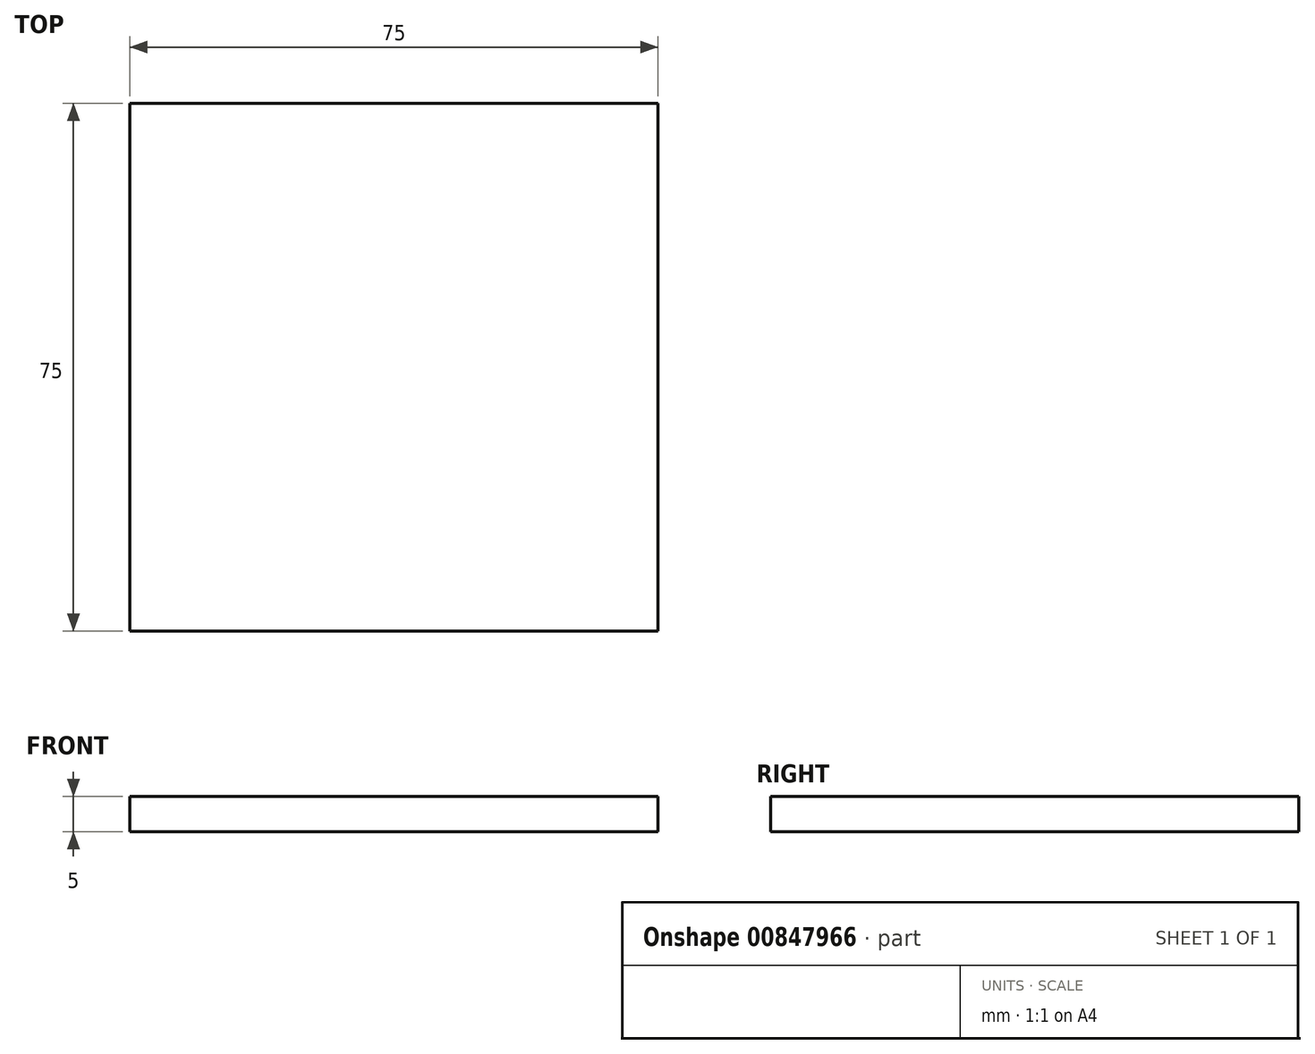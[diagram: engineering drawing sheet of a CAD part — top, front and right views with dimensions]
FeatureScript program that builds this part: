
annotation { "Feature Type Name" : "Feature", "Feature Type Description" : "" }
export const myFeature = defineFeature(function(context is Context, id is Id, definition is map)
    precondition{}
    {
        {
            var Q0;
            Q0=qCreatedBy(makeId("Top.planeOp"),FACE);
            var sketch = newSketch(context, id + "F0", { "sketchPlane" : qUnion([Q0])});
            skLineSegment(sketch, "E0.bottom", {"start": v(37.5, -37.5) * mm, "end": v(-37.5, -37.5) * mm});
            skLineSegment(sketch, "E0.top", {"start": v(37.5, 37.5) * mm, "end": v(-37.5, 37.5) * mm});
            skLineSegment(sketch, "E0.left", {"start": v(37.5, -37.5) * mm, "end": v(37.5, 37.5) * mm});
            skLineSegment(sketch, "E0.right", {"start": v(-37.5, -37.5) * mm, "end": v(-37.5, 37.5) * mm});
            skPoint(sketch, "E0.middle", {"position": v(0, 0) * mm});
            skSolve(sketch);
        }
        {
            var Q0;
            Q0 = qSketchRegion(id + "F0", true);
            extrude(context, id + "F1", {"entities" : qUnion([Q0]), "depth" : 5 * mm, "offsetDistance" : 25 * mm});
        }
    });
